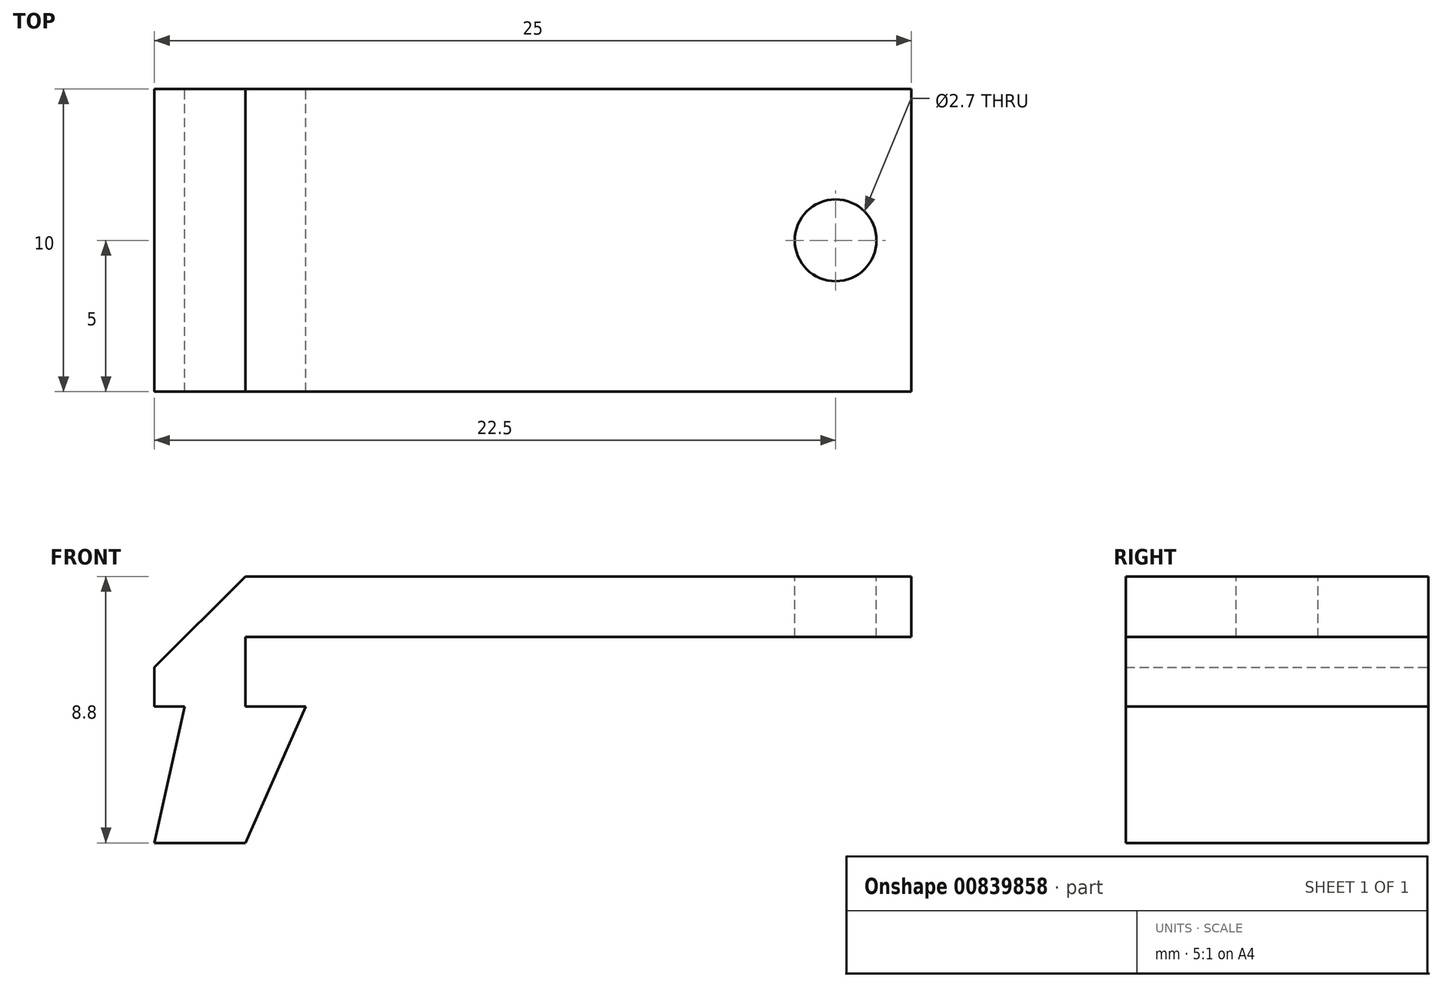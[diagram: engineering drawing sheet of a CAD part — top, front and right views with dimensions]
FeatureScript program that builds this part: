
annotation { "Feature Type Name" : "Feature", "Feature Type Description" : "" }
export const myFeature = defineFeature(function(context is Context, id is Id, definition is map)
    precondition{}
    {
        {
            var Q0;
            Q0=qCreatedBy(makeId("Front.planeOp"),FACE);
            var sketch = newSketch(context, id + "F0", { "sketchPlane" : qUnion([Q0])});
            skLineSegment(sketch, "E0", {"start": v(0, 0) * mm, "end": v(0, 0) * mm});
            skLineSegment(sketch, "E1", {"start": v(0, 0) * mm, "end": v(2, 4.5) * mm});
            skLineSegment(sketch, "E2", {"start": v(2, 4.5) * mm, "end": v(0, 4.5) * mm});
            skLineSegment(sketch, "E3", {"start": v(0, 4.5) * mm, "end": v(0, 6.8) * mm});
            skLineSegment(sketch, "E4", {"start": v(0, 6.8) * mm, "end": v(22, 6.8) * mm});
            skLineSegment(sketch, "E5", {"start": v(22, 6.8) * mm, "end": v(22, 8.8) * mm});
            skLineSegment(sketch, "E6", {"start": v(22, 8.8) * mm, "end": v(-3, 8.8) * mm});
            skLineSegment(sketch, "E7", {"start": v(-3, 8.8) * mm, "end": v(-3, 4.5) * mm});
            skLineSegment(sketch, "E8", {"start": v(-3, 4.5) * mm, "end": v(-2, 4.5) * mm});
            skLineSegment(sketch, "E9", {"start": v(-2, 4.5) * mm, "end": v(-3, 0) * mm});
            skLineSegment(sketch, "E10", {"start": v(-3, 0) * mm, "end": v(0, 0) * mm});
            skLineSegment(sketch, "E11", {"start": v(0, 4.5) * mm, "end": v(0, 0) * mm, "construction": true});
            skLineSegment(sketch, "E12", {"start": v(-3, 5.8) * mm, "end": v(0, 8.8) * mm});
            skSolve(sketch);
        }
        {
            var Q0;
            Q0=makeQuery(id+"F0.imprint","IMPRINT",FACE,{"disambiguationData":[TD([[makeQuery(id+"F0.imprint","IMPRINT",EDGE,{"derivedFrom":sQuery(id+"F0.wireOp",EDGE,"E1")}),1.0]])]});
            extrude(context, id + "F1", {"entities" : qUnion([Q0]), "depth" : 10 * mm, "offsetDistance" : 25 * mm});
        }
        {
            var Q0;
            Q0=makeQuery(id+"F1.opExtrude","SWEPT_FACE",FACE,{"disambiguationData":[OSD([sQuery(id+"F0.wireOp",EDGE,"E6")])]});
            var sketch = newSketch(context, id + "F2", { "sketchPlane" : qUnion([Q0])});
            skCircle(sketch, "E13", {"center": v(19.5, -5) * mm, "radius": 1.35 * mm});
            skLineSegment(sketch, "E14", {"start": v(18.15, 0) * mm, "end": v(18.15, -15.01) * mm, "construction": true});
            skLineSegment(sketch, "E15.direction1", {"start": v(19.5, -5) * mm, "end": v(44.5, -5) * mm, "construction": true});
            skLineSegment(sketch, "E15.direction2", {"start": v(19.5, -5) * mm, "end": v(19.5, -25) * mm, "construction": true});
            skSolve(sketch);
        }
        {
            var Q0;
            Q0=makeQuery(id+"F2.imprint","IMPRINT",FACE,{"disambiguationData":[TD([[makeQuery(id+"F2.imprint","IMPRINT",EDGE,{"derivedFrom":sQuery(id+"F2.wireOp",EDGE,"E13")}),1.0]])]});
            var Q1;
            Q1=makeQuery(id+"F2.imprint","IMPRINT",FACE,{"disambiguationData":[TD([[makeQuery(id+"F2.imprint","IMPRINT",EDGE,{"derivedFrom":sQuery(id+"F2.wireOp",EDGE,"E15.0.1.0")}),1.0]])]});
            var Q2;
            Q2=makeQuery(id+"F2.imprint","IMPRINT",FACE,{"disambiguationData":[TD([[makeQuery(id+"F2.imprint","IMPRINT",EDGE,{"derivedFrom":sQuery(id+"F2.wireOp",EDGE,"E15.0.2.0")}),1.0]])]});
            var Q3;
            Q3=makeQuery(id+"F2.imprint","IMPRINT",FACE,{"disambiguationData":[TD([[makeQuery(id+"F2.imprint","IMPRINT",EDGE,{"derivedFrom":sQuery(id+"F2.wireOp",EDGE,"E15.0.3.0")}),1.0]])]});
            var Q4;
            Q4=makeQuery(id+"F2.imprint","IMPRINT",FACE,{"disambiguationData":[TD([[makeQuery(id+"F2.imprint","IMPRINT",EDGE,{"derivedFrom":sQuery(id+"F2.wireOp",EDGE,"E15.0.4.0")}),1.0]])]});
            extrude(context, id + "F3", {"entities" : qUnion([Q0, Q1, Q2, Q3, Q4]), "operationType" : NewBodyOperationType.REMOVE, "oppositeDirection" : true, "depth" : 25 * mm, "offsetDistance" : 25 * mm});
        }
    });
